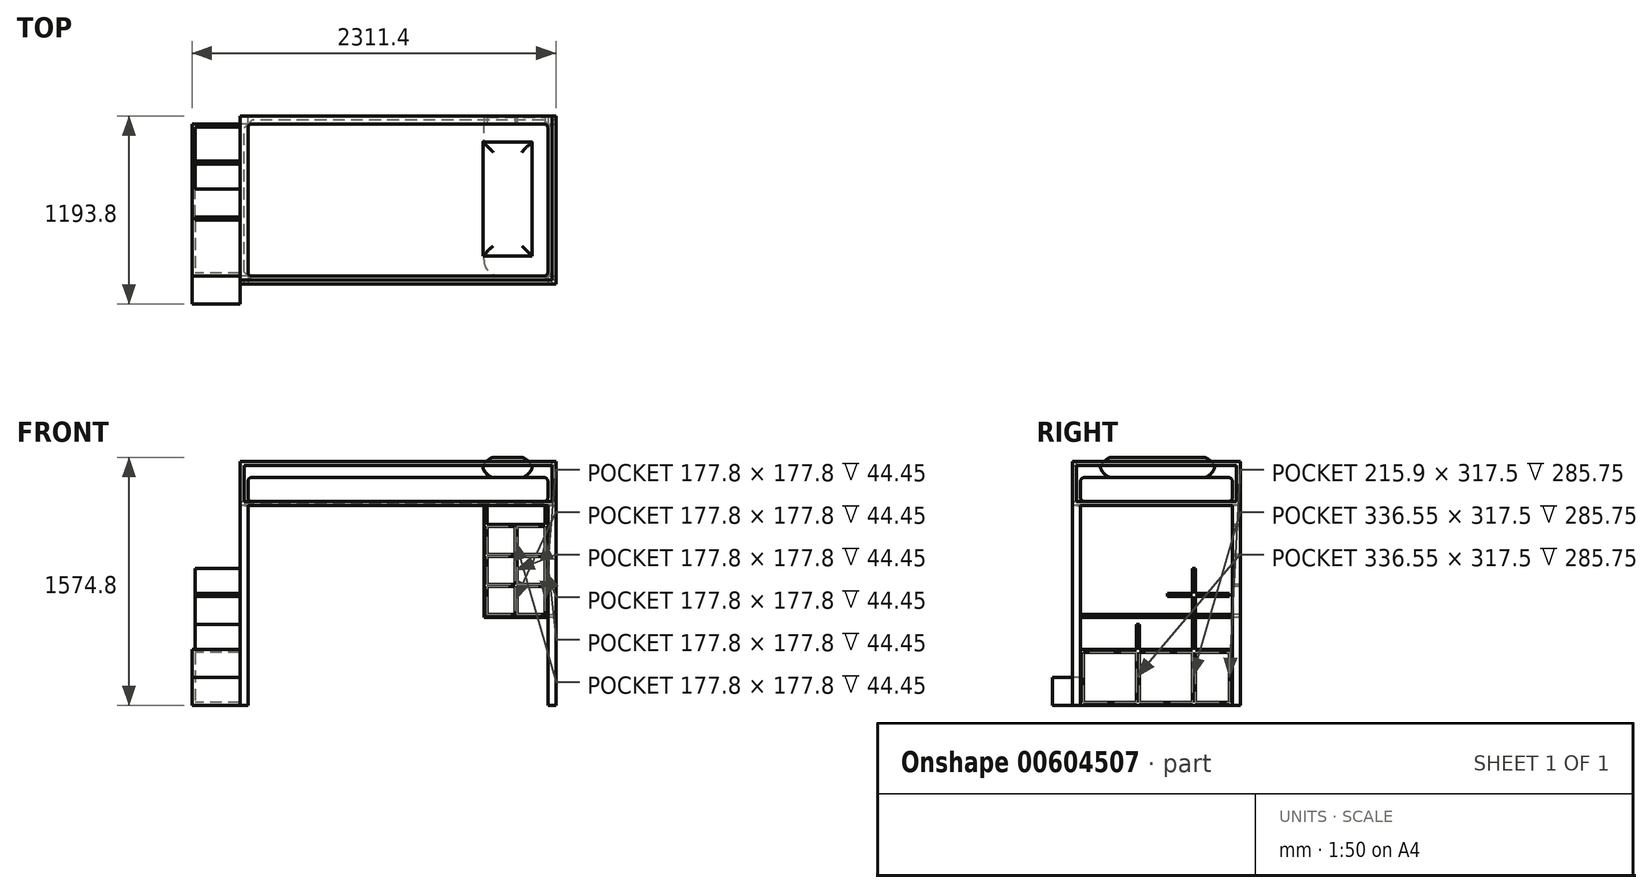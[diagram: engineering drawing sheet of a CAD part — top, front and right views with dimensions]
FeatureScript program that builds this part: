
annotation { "Feature Type Name" : "Feature", "Feature Type Description" : "" }
export const myFeature = defineFeature(function(context is Context, id is Id, definition is map)
    precondition{}
    {
        {
            var Q0;
            Q0=qCreatedBy(makeId("Top.planeOp"),FACE);
            var sketch = newSketch(context, id + "F0", { "sketchPlane" : qUnion([Q0])});
            skLineSegment(sketch, "E0.bottom", {"start": v(-952.5, 482.6) * mm, "end": v(952.5, 482.6) * mm});
            skLineSegment(sketch, "E0.top", {"start": v(-952.5, -482.6) * mm, "end": v(952.5, -482.6) * mm});
            skLineSegment(sketch, "E0.left", {"start": v(-952.5, 482.6) * mm, "end": v(-952.5, -482.6) * mm});
            skLineSegment(sketch, "E0.right", {"start": v(952.5, 482.6) * mm, "end": v(952.5, -482.6) * mm});
            skPoint(sketch, "E0.middle", {"position": v(0, 0) * mm});
            skLineSegment(sketch, "E1.bottom", {"start": v(-952.5, 482.6) * mm, "end": v(-1003.3, 482.6) * mm});
            skLineSegment(sketch, "E1.top", {"start": v(-952.5, 533.4) * mm, "end": v(-1003.3, 533.4) * mm});
            skLineSegment(sketch, "E1.left", {"start": v(-952.5, 482.6) * mm, "end": v(-952.5, 533.4) * mm});
            skLineSegment(sketch, "E1.right", {"start": v(-1003.3, 482.6) * mm, "end": v(-1003.3, 533.4) * mm});
            skLineSegment(sketch, "E2.bottom", {"start": v(-952.5, -482.6) * mm, "end": v(-1003.3, -482.6) * mm});
            skLineSegment(sketch, "E2.top", {"start": v(-952.5, -533.4) * mm, "end": v(-1003.3, -533.4) * mm});
            skLineSegment(sketch, "E2.left", {"start": v(-952.5, -482.6) * mm, "end": v(-952.5, -533.4) * mm});
            skLineSegment(sketch, "E2.right", {"start": v(-1003.3, -482.6) * mm, "end": v(-1003.3, -533.4) * mm});
            skLineSegment(sketch, "E3.bottom", {"start": v(952.5, 482.6) * mm, "end": v(1003.3, 482.6) * mm});
            skLineSegment(sketch, "E3.top", {"start": v(952.5, 533.4) * mm, "end": v(1003.3, 533.4) * mm});
            skLineSegment(sketch, "E3.left", {"start": v(952.5, 482.6) * mm, "end": v(952.5, 533.4) * mm});
            skLineSegment(sketch, "E3.right", {"start": v(1003.3, 482.6) * mm, "end": v(1003.3, 533.4) * mm});
            skLineSegment(sketch, "E4.bottom", {"start": v(952.5, -482.6) * mm, "end": v(1003.3, -482.6) * mm});
            skLineSegment(sketch, "E4.top", {"start": v(952.5, -533.4) * mm, "end": v(1003.3, -533.4) * mm});
            skLineSegment(sketch, "E4.left", {"start": v(952.5, -482.6) * mm, "end": v(952.5, -533.4) * mm});
            skLineSegment(sketch, "E4.right", {"start": v(1003.3, -482.6) * mm, "end": v(1003.3, -533.4) * mm});
            skSolve(sketch);
        }
        {
            var Q0;
            Q0=makeQuery(id+"F0.imprint","IMPRINT",FACE,{"disambiguationData":[TD([[makeQuery(id+"F0.imprint","IMPRINT",EDGE,{"derivedFrom":sQuery(id+"F0.wireOp",EDGE,"E1.bottom")}),-1.0]])]});
            var Q1;
            Q1=makeQuery(id+"F0.imprint","IMPRINT",FACE,{"disambiguationData":[TD([[makeQuery(id+"F0.imprint","IMPRINT",EDGE,{"derivedFrom":sQuery(id+"F0.wireOp",EDGE,"E2.bottom")}),1.0]])]});
            var Q2;
            Q2=makeQuery(id+"F0.imprint","IMPRINT",FACE,{"disambiguationData":[TD([[makeQuery(id+"F0.imprint","IMPRINT",EDGE,{"derivedFrom":sQuery(id+"F0.wireOp",EDGE,"E3.bottom")}),1.0]])]});
            var Q3;
            Q3=makeQuery(id+"F0.imprint","IMPRINT",FACE,{"disambiguationData":[TD([[makeQuery(id+"F0.imprint","IMPRINT",EDGE,{"derivedFrom":sQuery(id+"F0.wireOp",EDGE,"E4.bottom")}),-1.0]])]});
            extrude(context, id + "F1", {"entities" : qUnion([Q0, Q1, Q2, Q3]), "depth" : 1270 * mm});
        }
        {
            var Q0;
            Q0=makeQuery(id+"F1.opExtrude","SWEPT_FACE",FACE,{"disambiguationData":[OSD([sQuery(id+"F0.wireOp",EDGE,"E1.right")])]});
            cPlane(context, id + "F2", {"entities" : qUnion([Q0]), "cplaneType" : CPlaneType.OFFSET, "offset" : 304.8 * mm, "width" : 152.4 * mm, "height" : 152.4 * mm});
        }
        {
            var Q0;
            Q0=qCreatedBy(id+"F2.planeOp",FACE);
            var sketch = newSketch(context, id + "F3", { "sketchPlane" : qUnion([Q0])});
            skPoint(sketch, "E5.0", {"position": v(-482.6, 0) * mm});
            skPoint(sketch, "E6.0", {"position": v(482.6, 0) * mm});
            skLineSegment(sketch, "E7.bottom", {"start": v(-482.6, 0) * mm, "end": v(482.6, 0) * mm});
            skLineSegment(sketch, "E7.top", {"start": v(-482.6, 355.6) * mm, "end": v(482.6, 355.6) * mm});
            skLineSegment(sketch, "E7.left", {"start": v(-482.6, 0) * mm, "end": v(-482.6, 355.6) * mm});
            skLineSegment(sketch, "E7.right", {"start": v(482.6, 0) * mm, "end": v(482.6, 147.48) * mm});
            skLineSegment(sketch, "E8.bottom", {"start": v(-482.6, 355.6) * mm, "end": v(127, 355.6) * mm});
            skLineSegment(sketch, "E8.top", {"start": v(-482.6, 711.2) * mm, "end": v(127, 711.2) * mm});
            skLineSegment(sketch, "E8.left", {"start": v(-482.6, 355.6) * mm, "end": v(-482.6, 711.2) * mm});
            skLineSegment(sketch, "E8.right", {"start": v(127, 355.6) * mm, "end": v(127, 711.2) * mm});
            skLineSegment(sketch, "E9.bottom", {"start": v(-482.6, 711.2) * mm, "end": v(-228.6, 711.2) * mm});
            skLineSegment(sketch, "E9.top", {"start": v(-482.6, 1066.8) * mm, "end": v(-228.6, 1066.8) * mm});
            skLineSegment(sketch, "E9.left", {"start": v(-482.6, 711.2) * mm, "end": v(-482.6, 1066.8) * mm});
            skLineSegment(sketch, "E9.right", {"start": v(-228.6, 711.2) * mm, "end": v(-228.6, 1066.8) * mm});
            skLineSegment(sketch, "E10.bottom", {"start": v(127, 355.6) * mm, "end": v(304.8, 355.6) * mm});
            skLineSegment(sketch, "E10.top", {"start": v(127, 533.4) * mm, "end": v(304.8, 533.4) * mm});
            skLineSegment(sketch, "E10.left", {"start": v(127, 355.6) * mm, "end": v(127, 533.4) * mm});
            skLineSegment(sketch, "E10.right", {"start": v(304.8, 355.6) * mm, "end": v(304.8, 533.4) * mm});
            skLineSegment(sketch, "E11.bottom", {"start": v(482.6, 0) * mm, "end": v(660.4, 0) * mm});
            skLineSegment(sketch, "E11.top", {"start": v(482.6, 177.8) * mm, "end": v(660.4, 177.8) * mm});
            skLineSegment(sketch, "E11.left", {"start": v(482.6, 0) * mm, "end": v(482.6, 177.8) * mm});
            skLineSegment(sketch, "E11.right", {"start": v(660.4, 0) * mm, "end": v(660.4, 177.8) * mm});
            skLineSegment(sketch, "E12.bottom", {"start": v(-228.6, 711.2) * mm, "end": v(-50.8, 711.2) * mm});
            skLineSegment(sketch, "E12.top", {"start": v(-228.6, 889) * mm, "end": v(-50.8, 889) * mm});
            skLineSegment(sketch, "E12.left", {"start": v(-228.6, 711.2) * mm, "end": v(-228.6, 889) * mm});
            skLineSegment(sketch, "E12.right", {"start": v(-50.8, 711.2) * mm, "end": v(-50.8, 889) * mm});
            skLineSegment(sketch, "E13", {"start": v(482.6, 355.6) * mm, "end": v(482.6, 177.8) * mm});
            skSolve(sketch);
        }
        {
            var Q0;
            Q0=makeQuery(id+"F3.imprint","IMPRINT",FACE,{"disambiguationData":[TD([[makeQuery(id+"F3.imprint","IMPRINT",EDGE,{"derivedFrom":sQuery(id+"F3.wireOp",EDGE,"E9.bottom")}),1.0]])]});
            var Q1;
            Q1=makeQuery(id+"F3.imprint","IMPRINT",FACE,{"disambiguationData":[TD([[makeQuery(id+"F3.imprint","IMPRINT",EDGE,{"derivedFrom":sQuery(id+"F3.wireOp",EDGE,"E12.bottom")}),1.0]])]});
            var Q2;
            Q2=makeQuery(id+"F3.imprint","IMPRINT",FACE,{"disambiguationData":[TD([[makeQuery(id+"F3.imprint","IMPRINT",EDGE,{"derivedFrom":sQuery(id+"F3.wireOp",EDGE,"E8.bottom")}),1.0]])]});
            var Q3;
            Q3=makeQuery(id+"F3.imprint","IMPRINT",FACE,{"disambiguationData":[TD([[makeQuery(id+"F3.imprint","IMPRINT",EDGE,{"derivedFrom":sQuery(id+"F3.wireOp",EDGE,"E10.bottom")}),1.0]])]});
            var Q4;
            {var subQ1=sQuery(id+"F3.wireOp",EDGE,"E7.bottom");Q4=makeQuery(id+"F3.imprint","IMPRINT",FACE,{"disambiguationData":[TD([[makeQuery(id+"F3.imprint","IMPRINT",EDGE,{"derivedFrom":subQ1}),1.0]])]});}
            var Q5;
            {var subQ3=sQuery(id+"F3.wireOp",EDGE,"E11.bottom");Q5=makeQuery(id+"F3.imprint","IMPRINT",FACE,{"disambiguationData":[TD([[makeQuery(id+"F3.imprint","IMPRINT",EDGE,{"derivedFrom":subQ3}),1.0]])]});}
            extrude(context, id + "F4", {"entities" : qUnion([Q0, Q1, Q2, Q3, Q4, Q5]), "oppositeDirection" : true, "depth" : 19.05 * mm});
        }
        {
            var Q0;
            Q0=makeQuery(id+"F4.opExtrude","CAP_FACE",FACE,{"disambiguationData":[OSD([sQuery(id+"F3.wireOp",EDGE,"E7.bottom"),sQuery(id+"F3.wireOp",EDGE,"E7.top"),sQuery(id+"F3.wireOp",EDGE,"E7.left"),sQuery(id+"F3.wireOp",EDGE,"E8.top"),sQuery(id+"F3.wireOp",EDGE,"E8.left"),sQuery(id+"F3.wireOp",EDGE,"E8.right"),sQuery(id+"F3.wireOp",EDGE,"E9.top"),sQuery(id+"F3.wireOp",EDGE,"E9.left"),sQuery(id+"F3.wireOp",EDGE,"E9.right"),sQuery(id+"F3.wireOp",EDGE,"E10.top"),sQuery(id+"F3.wireOp",EDGE,"E10.right"),sQuery(id+"F3.wireOp",EDGE,"E11.bottom"),sQuery(id+"F3.wireOp",EDGE,"E11.top"),sQuery(id+"F3.wireOp",EDGE,"E11.right"),sQuery(id+"F3.wireOp",EDGE,"E12.top"),sQuery(id+"F3.wireOp",EDGE,"E12.right"),sQuery(id+"F3.wireOp",EDGE,"E13")])],"isStart":false});
            var sketch = newSketch(context, id + "F5", { "sketchPlane" : qUnion([Q0])});
            skLineSegment(sketch, "E14.0", {"start": v(-463.55, 19.05) * mm, "end": v(463.55, 19.05) * mm});
            skLineSegment(sketch, "E14.1", {"start": v(69.85, 869.95) * mm, "end": v(69.85, 692.15) * mm});
            skLineSegment(sketch, "E14.2", {"start": v(247.65, 869.95) * mm, "end": v(69.85, 869.95) * mm});
            skLineSegment(sketch, "E14.3", {"start": v(247.65, 1047.75) * mm, "end": v(247.65, 869.95) * mm});
            skLineSegment(sketch, "E14.4", {"start": v(463.55, 1047.75) * mm, "end": v(247.65, 1047.75) * mm});
            skLineSegment(sketch, "E14.5", {"start": v(69.85, 692.15) * mm, "end": v(-107.95, 692.15) * mm});
            skLineSegment(sketch, "E14.6", {"start": v(463.55, 19.05) * mm, "end": v(463.55, 1047.75) * mm});
            skLineSegment(sketch, "E14.7", {"start": v(-107.95, 692.15) * mm, "end": v(-107.95, 514.35) * mm});
            skLineSegment(sketch, "E14.8", {"start": v(-107.95, 514.35) * mm, "end": v(-285.75, 514.35) * mm});
            skLineSegment(sketch, "E14.9", {"start": v(-285.75, 514.35) * mm, "end": v(-285.75, 336.55) * mm});
            skLineSegment(sketch, "E14.10", {"start": v(-285.75, 336.55) * mm, "end": v(-463.55, 336.55) * mm});
            skLineSegment(sketch, "E14.11", {"start": v(-463.55, 336.55) * mm, "end": v(-463.55, 19.05) * mm});
            skLineSegment(sketch, "E15.0.0", {"start": v(482.6, 0) * mm, "end": v(482.6, 1066.8) * mm});
            skLineSegment(sketch, "E15.0.1", {"start": v(482.6, 1066.8) * mm, "end": v(228.6, 1066.8) * mm});
            skLineSegment(sketch, "E15.0.2", {"start": v(228.6, 1066.8) * mm, "end": v(228.6, 889) * mm});
            skLineSegment(sketch, "E15.0.3", {"start": v(228.6, 889) * mm, "end": v(50.8, 889) * mm});
            skLineSegment(sketch, "E15.0.4", {"start": v(50.8, 889) * mm, "end": v(50.8, 711.2) * mm});
            skLineSegment(sketch, "E15.0.5", {"start": v(50.8, 711.2) * mm, "end": v(-127, 711.2) * mm});
            skLineSegment(sketch, "E15.0.6", {"start": v(-127, 711.2) * mm, "end": v(-127, 533.4) * mm});
            skLineSegment(sketch, "E15.0.7", {"start": v(-127, 533.4) * mm, "end": v(-304.8, 533.4) * mm});
            skLineSegment(sketch, "E15.0.8", {"start": v(-304.8, 533.4) * mm, "end": v(-304.8, 355.6) * mm});
            skLineSegment(sketch, "E15.0.9", {"start": v(-304.8, 355.6) * mm, "end": v(-482.6, 355.6) * mm});
            skLineSegment(sketch, "E15.0.10", {"start": v(-482.6, 355.6) * mm, "end": v(-482.6, 177.8) * mm});
            skLineSegment(sketch, "E15.0.11", {"start": v(-482.6, 177.8) * mm, "end": v(-660.4, 177.8) * mm});
            skLineSegment(sketch, "E15.0.12", {"start": v(-660.4, 177.8) * mm, "end": v(-660.4, 0) * mm});
            skLineSegment(sketch, "E15.0.13", {"start": v(-660.4, 0) * mm, "end": v(482.6, 0) * mm});
            skSolve(sketch);
        }
        {
            var Q0;
            Q0=makeQuery(id+"F5.imprint","IMPRINT",FACE,{"disambiguationData":[TD([[makeQuery(id+"F5.imprint","IMPRINT",EDGE,{"derivedFrom":sQuery(id+"F5.wireOp",EDGE,"E14.0")}),-1.0]])]});
            extrude(context, id + "F6", {"entities" : qUnion([Q0]), "operationType" : NewBodyOperationType.ADD, "depth" : 285.75 * mm});
        }
        {
            var Q0;
            Q0=makeQuery(id+"F4.opExtrude","CAP_FACE",FACE,{"disambiguationData":[OSD([sQuery(id+"F3.wireOp",EDGE,"E7.bottom"),sQuery(id+"F3.wireOp",EDGE,"E7.top"),sQuery(id+"F3.wireOp",EDGE,"E7.left"),sQuery(id+"F3.wireOp",EDGE,"E8.top"),sQuery(id+"F3.wireOp",EDGE,"E8.left"),sQuery(id+"F3.wireOp",EDGE,"E8.right"),sQuery(id+"F3.wireOp",EDGE,"E9.top"),sQuery(id+"F3.wireOp",EDGE,"E9.left"),sQuery(id+"F3.wireOp",EDGE,"E9.right"),sQuery(id+"F3.wireOp",EDGE,"E10.top"),sQuery(id+"F3.wireOp",EDGE,"E10.right"),sQuery(id+"F3.wireOp",EDGE,"E11.bottom"),sQuery(id+"F3.wireOp",EDGE,"E11.top"),sQuery(id+"F3.wireOp",EDGE,"E11.right"),sQuery(id+"F3.wireOp",EDGE,"E12.top"),sQuery(id+"F3.wireOp",EDGE,"E12.right"),sQuery(id+"F3.wireOp",EDGE,"E13")])],"isStart":false});
            var sketch = newSketch(context, id + "F7", { "sketchPlane" : qUnion([Q0])});
            skLineSegment(sketch, "E16.bottom", {"start": v(-285.75, 336.55) * mm, "end": v(463.55, 336.55) * mm});
            skLineSegment(sketch, "E16.top", {"start": v(-285.75, 355.6) * mm, "end": v(463.55, 355.6) * mm});
            skLineSegment(sketch, "E16.left", {"start": v(-285.75, 336.55) * mm, "end": v(-285.75, 355.6) * mm});
            skLineSegment(sketch, "E16.right", {"start": v(463.55, 336.55) * mm, "end": v(463.55, 355.6) * mm});
            skLineSegment(sketch, "E17.bottom", {"start": v(-107.95, 514.35) * mm, "end": v(-127, 514.35) * mm});
            skLineSegment(sketch, "E17.top", {"start": v(-107.95, 19.05) * mm, "end": v(-127, 19.05) * mm});
            skLineSegment(sketch, "E17.left", {"start": v(-107.95, 514.35) * mm, "end": v(-107.95, 19.05) * mm});
            skLineSegment(sketch, "E17.right", {"start": v(-127, 514.35) * mm, "end": v(-127, 19.05) * mm});
            skLineSegment(sketch, "E18.bottom", {"start": v(247.65, 869.95) * mm, "end": v(228.6, 869.95) * mm});
            skLineSegment(sketch, "E18.top", {"start": v(247.65, 19.05) * mm, "end": v(228.6, 19.05) * mm});
            skLineSegment(sketch, "E18.left", {"start": v(247.65, 869.95) * mm, "end": v(247.65, 19.05) * mm});
            skLineSegment(sketch, "E18.right", {"start": v(228.6, 869.95) * mm, "end": v(228.6, 19.05) * mm});
            skLineSegment(sketch, "E19.bottom", {"start": v(69.85, 692.15) * mm, "end": v(463.55, 692.15) * mm});
            skLineSegment(sketch, "E19.top", {"start": v(69.85, 711.2) * mm, "end": v(463.55, 711.2) * mm});
            skLineSegment(sketch, "E19.left", {"start": v(69.85, 692.15) * mm, "end": v(69.85, 711.2) * mm});
            skLineSegment(sketch, "E19.right", {"start": v(463.55, 692.15) * mm, "end": v(463.55, 711.2) * mm});
            skSolve(sketch);
        }
        {
            var Q0;
            Q0=qSketchRegion(id+"F7",true);
            extrude(context, id + "F8", {"entities" : qUnion([Q0]), "operationType" : NewBodyOperationType.ADD, "depth" : 285.75 * mm});
        }
        {
            var Q0;
            Q0=makeQuery(id+"F1.opExtrude","CAP_FACE",FACE,{"disambiguationData":[OSD([sQuery(id+"F0.wireOp",EDGE,"E1.bottom"),sQuery(id+"F0.wireOp",EDGE,"E1.top"),sQuery(id+"F0.wireOp",EDGE,"E1.left"),sQuery(id+"F0.wireOp",EDGE,"E1.right")])],"isStart":false});
            var sketch = newSketch(context, id + "F9", { "sketchPlane" : qUnion([Q0])});
            skPoint(sketch, "E20.0", {"position": v(1003.3, -533.4) * mm});
            skPoint(sketch, "E21.0", {"position": v(-1003.3, 533.4) * mm});
            skLineSegment(sketch, "E22.bottom", {"start": v(-1003.3, 533.4) * mm, "end": v(1003.3, 533.4) * mm});
            skLineSegment(sketch, "E22.top", {"start": v(-1003.3, -533.4) * mm, "end": v(1003.3, -533.4) * mm});
            skLineSegment(sketch, "E22.left", {"start": v(-1003.3, 533.4) * mm, "end": v(-1003.3, -533.4) * mm});
            skLineSegment(sketch, "E22.right", {"start": v(1003.3, 533.4) * mm, "end": v(1003.3, -533.4) * mm});
            skLineSegment(sketch, "E23.0.0", {"start": v(1003.3, -482.6) * mm, "end": v(952.5, -482.6) * mm});
            skLineSegment(sketch, "E23.0.1", {"start": v(952.5, -482.6) * mm, "end": v(952.5, -533.4) * mm});
            skLineSegment(sketch, "E23.0.2", {"start": v(952.5, -533.4) * mm, "end": v(1003.3, -533.4) * mm});
            skLineSegment(sketch, "E23.0.3", {"start": v(1003.3, -533.4) * mm, "end": v(1003.3, -482.6) * mm});
            skLineSegment(sketch, "E24.0.0", {"start": v(1003.3, 533.4) * mm, "end": v(952.5, 533.4) * mm});
            skLineSegment(sketch, "E24.0.1", {"start": v(952.5, 533.4) * mm, "end": v(952.5, 482.6) * mm});
            skLineSegment(sketch, "E24.0.2", {"start": v(952.5, 482.6) * mm, "end": v(1003.3, 482.6) * mm});
            skLineSegment(sketch, "E24.0.3", {"start": v(1003.3, 482.6) * mm, "end": v(1003.3, 533.4) * mm});
            skLineSegment(sketch, "E25.0.0", {"start": v(-952.5, -533.4) * mm, "end": v(-952.5, -482.6) * mm});
            skLineSegment(sketch, "E25.0.1", {"start": v(-952.5, -482.6) * mm, "end": v(-1003.3, -482.6) * mm});
            skLineSegment(sketch, "E25.0.2", {"start": v(-1003.3, -482.6) * mm, "end": v(-1003.3, -533.4) * mm});
            skLineSegment(sketch, "E25.0.3", {"start": v(-1003.3, -533.4) * mm, "end": v(-952.5, -533.4) * mm});
            skLineSegment(sketch, "E26.0.0", {"start": v(-952.5, 482.6) * mm, "end": v(-952.5, 533.4) * mm});
            skLineSegment(sketch, "E26.0.1", {"start": v(-952.5, 533.4) * mm, "end": v(-1003.3, 533.4) * mm});
            skLineSegment(sketch, "E26.0.2", {"start": v(-1003.3, 533.4) * mm, "end": v(-1003.3, 482.6) * mm});
            skLineSegment(sketch, "E26.0.3", {"start": v(-1003.3, 482.6) * mm, "end": v(-952.5, 482.6) * mm});
            skPoint(sketch, "E27.firstSnap0", {"position": v(952.5, -508) * mm});
            skPoint(sketch, "E27.firstSnap1", {"position": v(977.9, -482.6) * mm});
            skPoint(sketch, "E27.oppositeSnap0", {"position": v(-1003.3, 508) * mm});
            skPoint(sketch, "E27.oppositeSnap1", {"position": v(-977.9, 533.4) * mm});
            skLineSegment(sketch, "E27.bottom", {"start": v(977.9, -508) * mm, "end": v(-977.9, -508) * mm});
            skLineSegment(sketch, "E27.top", {"start": v(977.9, 508) * mm, "end": v(-977.9, 508) * mm});
            skLineSegment(sketch, "E27.left", {"start": v(977.9, -508) * mm, "end": v(977.9, 508) * mm});
            skLineSegment(sketch, "E27.right", {"start": v(-977.9, -508) * mm, "end": v(-977.9, 508) * mm});
            skSolve(sketch);
        }
        {
            var Q0;
            Q0=qSketchRegion(id+"F9",true);
            extrude(context, id + "F10", {"entities" : qUnion([Q0]), "depth" : 25.4 * mm});
        }
        {
            var Q0;
            Q0=makeQuery(id+"F10.opExtrude","CAP_FACE",FACE,{"disambiguationData":[OSD([sQuery(id+"F9.wireOp",EDGE,"E22.bottom"),sQuery(id+"F9.wireOp",EDGE,"E22.top"),sQuery(id+"F9.wireOp",EDGE,"E22.left"),sQuery(id+"F9.wireOp",EDGE,"E22.right")])],"isStart":false});
            var sketch = newSketch(context, id + "F11", { "sketchPlane" : qUnion([Q0])});
            skPoint(sketch, "E28.0", {"position": v(-952.5, 482.6) * mm});
            skPoint(sketch, "E29.0", {"position": v(952.5, -482.6) * mm});
            skLineSegment(sketch, "E30.bottom", {"start": v(-952.5, 482.6) * mm, "end": v(952.5, 482.6) * mm});
            skLineSegment(sketch, "E30.top", {"start": v(-952.5, -482.6) * mm, "end": v(952.5, -482.6) * mm});
            skLineSegment(sketch, "E30.left", {"start": v(-952.5, 482.6) * mm, "end": v(-952.5, -482.6) * mm});
            skLineSegment(sketch, "E30.right", {"start": v(952.5, 482.6) * mm, "end": v(952.5, -482.6) * mm});
            skSolve(sketch);
        }
        {
            var Q0;
            Q0=makeQuery(id+"F11.imprint","IMPRINT",FACE,{"disambiguationData":[TD([[makeQuery(id+"F11.imprint","IMPRINT",EDGE,{"derivedFrom":sQuery(id+"F11.wireOp",EDGE,"E30.bottom")}),-1.0]])]});
            extrude(context, id + "F12", {"entities" : qUnion([Q0]), "depth" : 152.4 * mm});
        }
        {
            var Q0;
            Q0=makeQuery(id+"F12.opExtrude","SWEPT_EDGE",EDGE,{"disambiguationData":[OSD([sQuery(id+"F11.wireOp",EDGE,"E30.top"),sQuery(id+"F11.wireOp",EDGE,"E30.left")])]});
            var Q1;
            Q1=makeQuery(id+"F12.opExtrude","SWEPT_EDGE",EDGE,{"disambiguationData":[OSD([sQuery(id+"F11.wireOp",EDGE,"E30.top"),sQuery(id+"F11.wireOp",EDGE,"E30.right")])]});
            var Q2;
            Q2=makeQuery(id+"F12.opExtrude","SWEPT_EDGE",EDGE,{"disambiguationData":[OSD([sQuery(id+"F11.wireOp",EDGE,"E30.bottom"),sQuery(id+"F11.wireOp",EDGE,"E30.right")])]});
            var Q3;
            Q3=makeQuery(id+"F12.opExtrude","SWEPT_EDGE",EDGE,{"disambiguationData":[OSD([sQuery(id+"F11.wireOp",EDGE,"E30.bottom"),sQuery(id+"F11.wireOp",EDGE,"E30.left")])]});
            var Q4;
            Q4=makeQuery(id+"F12.opExtrude","CAP_EDGE",EDGE,{"disambiguationData":[OSD([sQuery(id+"F11.wireOp",EDGE,"E30.left")])],"isStart":false});
            var Q5;
            Q5=makeQuery(id+"F12.opExtrude","CAP_EDGE",EDGE,{"disambiguationData":[OSD([sQuery(id+"F11.wireOp",EDGE,"E30.bottom")])],"isStart":false});
            var Q6;
            Q6=makeQuery(id+"F12.opExtrude","CAP_EDGE",EDGE,{"disambiguationData":[OSD([sQuery(id+"F11.wireOp",EDGE,"E30.right")])],"isStart":false});
            var Q7;
            Q7=makeQuery(id+"F12.opExtrude","CAP_EDGE",EDGE,{"disambiguationData":[OSD([sQuery(id+"F11.wireOp",EDGE,"E30.top")])],"isStart":false});
            var Q8;
            Q8=makeQuery(id+"F12.opExtrude","CAP_EDGE",EDGE,{"disambiguationData":[OSD([sQuery(id+"F11.wireOp",EDGE,"E30.top")])],"isStart":true});
            var Q9;
            Q9=makeQuery(id+"F12.opExtrude","CAP_EDGE",EDGE,{"disambiguationData":[OSD([sQuery(id+"F11.wireOp",EDGE,"E30.right")])],"isStart":true});
            var Q10;
            Q10=makeQuery(id+"F12.opExtrude","CAP_EDGE",EDGE,{"disambiguationData":[OSD([sQuery(id+"F11.wireOp",EDGE,"E30.bottom")])],"isStart":true});
            var Q11;
            Q11=makeQuery(id+"F12.opExtrude","CAP_EDGE",EDGE,{"disambiguationData":[OSD([sQuery(id+"F11.wireOp",EDGE,"E30.left")])],"isStart":true});
            fillet(context, id + "F13", {"entities" : qUnion([Q0, Q1, Q2, Q3, Q4, Q5, Q6, Q7, Q8, Q9, Q10, Q11]), "radius" : 25.4 * mm, "tangentPropagation" : true, "allowEdgeOverflow" : false});
        }
        {
            var Q0;
            Q0=makeQuery(id+"F10.opExtrude","CAP_FACE",FACE,{"disambiguationData":[OSD([sQuery(id+"F9.wireOp",EDGE,"E22.bottom"),sQuery(id+"F9.wireOp",EDGE,"E22.top"),sQuery(id+"F9.wireOp",EDGE,"E22.left"),sQuery(id+"F9.wireOp",EDGE,"E22.right"),sQuery(id+"F9.wireOp",EDGE,"E23.0.2"),sQuery(id+"F9.wireOp",EDGE,"E23.0.3"),sQuery(id+"F9.wireOp",EDGE,"E24.0.0"),sQuery(id+"F9.wireOp",EDGE,"E24.0.3"),sQuery(id+"F9.wireOp",EDGE,"E25.0.2"),sQuery(id+"F9.wireOp",EDGE,"E25.0.3"),sQuery(id+"F9.wireOp",EDGE,"E26.0.1"),sQuery(id+"F9.wireOp",EDGE,"E26.0.2"),sQuery(id+"F9.wireOp",EDGE,"E27.bottom"),sQuery(id+"F9.wireOp",EDGE,"E27.top"),sQuery(id+"F9.wireOp",EDGE,"E27.left"),sQuery(id+"F9.wireOp",EDGE,"E27.right")])],"isStart":true});
            var sketch = newSketch(context, id + "F14", { "sketchPlane" : qUnion([Q0])});
            skLineSegment(sketch, "E31.0", {"start": v(977.9, 508) * mm, "end": v(-977.9, 508) * mm});
            skLineSegment(sketch, "E32.0", {"start": v(-977.9, 508) * mm, "end": v(-977.9, -508) * mm});
            skLineSegment(sketch, "E33", {"start": v(-977.9, 508) * mm, "end": v(-927.1, 508) * mm});
            skLineSegment(sketch, "E34", {"start": v(-927.1, 508) * mm, "end": v(-977.9, 457.2) * mm});
            skLineSegment(sketch, "E35", {"start": v(-977.9, 457.2) * mm, "end": v(-977.9, 508) * mm});
            skLineSegment(sketch, "E36", {"start": v(-977.9, -508) * mm, "end": v(-977.9, -457.2) * mm});
            skLineSegment(sketch, "E37", {"start": v(-977.9, -457.2) * mm, "end": v(-927.1, -508) * mm});
            skLineSegment(sketch, "E38", {"start": v(-927.1, -508) * mm, "end": v(-977.9, -508) * mm});
            skLineSegment(sketch, "E39", {"start": v(977.9, -508) * mm, "end": v(927.1, -508) * mm});
            skLineSegment(sketch, "E40", {"start": v(927.1, -508) * mm, "end": v(977.9, -457.2) * mm});
            skLineSegment(sketch, "E41", {"start": v(977.9, -457.2) * mm, "end": v(977.9, -508) * mm});
            skLineSegment(sketch, "E42", {"start": v(977.9, 508) * mm, "end": v(927.1, 508) * mm});
            skLineSegment(sketch, "E43", {"start": v(927.1, 508) * mm, "end": v(977.9, 457.2) * mm});
            skLineSegment(sketch, "E44", {"start": v(977.9, 457.2) * mm, "end": v(977.9, 508) * mm});
            skLineSegment(sketch, "E45", {"start": v(927.1, 508) * mm, "end": v(977.9, 508) * mm});
            skLineSegment(sketch, "E46", {"start": v(977.9, 508) * mm, "end": v(977.9, 457.2) * mm});
            skSolve(sketch);
        }
        {
            var Q0;
            Q0=qSketchRegion(id+"F14",true);
            extrude(context, id + "F15", {"entities" : qUnion([Q0]), "operationType" : NewBodyOperationType.ADD, "oppositeDirection" : true, "depth" : 6.35 * mm});
        }
        {
            var Q0;
            Q0=makeQuery(id+"F15.opExtrude","CAP_FACE",FACE,{"disambiguationData":[OSD([sQuery(id+"F14.wireOp",EDGE,"E33"),sQuery(id+"F14.wireOp",EDGE,"E34"),sQuery(id+"F14.wireOp",EDGE,"E35")])],"isStart":false});
            var sketch = newSketch(context, id + "F16", { "sketchPlane" : qUnion([Q0])});
            skLineSegment(sketch, "E47.0.0", {"start": v(-977.9, 457.2) * mm, "end": v(-927.1, 508) * mm});
            skLineSegment(sketch, "E47.0.1", {"start": v(-927.1, 508) * mm, "end": v(-977.9, 508) * mm});
            skLineSegment(sketch, "E47.0.2", {"start": v(-977.9, 508) * mm, "end": v(-977.9, 457.2) * mm});
            skLineSegment(sketch, "E48.0.0", {"start": v(927.1, -508) * mm, "end": v(977.9, -508) * mm});
            skLineSegment(sketch, "E48.0.1", {"start": v(977.9, -508) * mm, "end": v(977.9, -457.2) * mm});
            skLineSegment(sketch, "E48.0.2", {"start": v(977.9, -457.2) * mm, "end": v(927.1, -508) * mm});
            skLineSegment(sketch, "E49.bottom", {"start": v(-977.9, 508) * mm, "end": v(977.9, 508) * mm});
            skLineSegment(sketch, "E49.top", {"start": v(-977.9, -508) * mm, "end": v(977.9, -508) * mm});
            skLineSegment(sketch, "E49.left", {"start": v(-977.9, 508) * mm, "end": v(-977.9, -508) * mm});
            skLineSegment(sketch, "E49.right", {"start": v(977.9, 508) * mm, "end": v(977.9, -508) * mm});
            skSolve(sketch);
        }
        {
            var Q0;
            Q0=qSketchRegion(id+"F16",true);
            extrude(context, id + "F17", {"entities" : qUnion([Q0]), "depth" : 19.05 * mm});
        }
        {
            var Q0;
            Q0=makeQuery(id+"F10.opExtrude","CAP_FACE",FACE,{"disambiguationData":[OSD([sQuery(id+"F9.wireOp",EDGE,"E22.bottom"),sQuery(id+"F9.wireOp",EDGE,"E22.top"),sQuery(id+"F9.wireOp",EDGE,"E22.left"),sQuery(id+"F9.wireOp",EDGE,"E22.right"),sQuery(id+"F9.wireOp",EDGE,"E23.0.2"),sQuery(id+"F9.wireOp",EDGE,"E23.0.3"),sQuery(id+"F9.wireOp",EDGE,"E24.0.0"),sQuery(id+"F9.wireOp",EDGE,"E24.0.3"),sQuery(id+"F9.wireOp",EDGE,"E25.0.2"),sQuery(id+"F9.wireOp",EDGE,"E25.0.3"),sQuery(id+"F9.wireOp",EDGE,"E26.0.1"),sQuery(id+"F9.wireOp",EDGE,"E26.0.2"),sQuery(id+"F9.wireOp",EDGE,"E27.bottom"),sQuery(id+"F9.wireOp",EDGE,"E27.top"),sQuery(id+"F9.wireOp",EDGE,"E27.left"),sQuery(id+"F9.wireOp",EDGE,"E27.right")])],"isStart":false});
            var sketch = newSketch(context, id + "F18", { "sketchPlane" : qUnion([Q0])});
            skLineSegment(sketch, "E50.bottom", {"start": v(1003.3, -533.4) * mm, "end": v(977.9, -533.4) * mm});
            skLineSegment(sketch, "E50.top", {"start": v(1003.3, -508) * mm, "end": v(977.9, -508) * mm});
            skLineSegment(sketch, "E50.left", {"start": v(1003.3, -533.4) * mm, "end": v(1003.3, -508) * mm});
            skLineSegment(sketch, "E50.right", {"start": v(977.9, -533.4) * mm, "end": v(977.9, -508) * mm});
            skLineSegment(sketch, "E51.bottom", {"start": v(1003.3, 533.4) * mm, "end": v(977.9, 533.4) * mm});
            skLineSegment(sketch, "E51.top", {"start": v(1003.3, 508) * mm, "end": v(977.9, 508) * mm});
            skLineSegment(sketch, "E51.left", {"start": v(1003.3, 533.4) * mm, "end": v(1003.3, 508) * mm});
            skLineSegment(sketch, "E51.right", {"start": v(977.9, 533.4) * mm, "end": v(977.9, 508) * mm});
            skLineSegment(sketch, "E52.bottom", {"start": v(-1003.3, -533.4) * mm, "end": v(-977.9, -533.4) * mm});
            skLineSegment(sketch, "E52.top", {"start": v(-1003.3, -508) * mm, "end": v(-977.9, -508) * mm});
            skLineSegment(sketch, "E52.left", {"start": v(-1003.3, -533.4) * mm, "end": v(-1003.3, -508) * mm});
            skLineSegment(sketch, "E52.right", {"start": v(-977.9, -533.4) * mm, "end": v(-977.9, -508) * mm});
            skSolve(sketch);
        }
        {
            var Q0;
            Q0=qSketchRegion(id+"F18",true);
            extrude(context, id + "F19", {"entities" : qUnion([Q0]), "operationType" : NewBodyOperationType.ADD, "depth" : 254 * mm});
        }
        {
            var Q0;
            Q0=makeQuery(id+"F19.opExtrude","CAP_FACE",FACE,{"disambiguationData":[OSD([sQuery(id+"F18.wireOp",EDGE,"E51.bottom"),sQuery(id+"F18.wireOp",EDGE,"E51.top"),sQuery(id+"F18.wireOp",EDGE,"E51.left"),sQuery(id+"F18.wireOp",EDGE,"E51.right")])],"isStart":false});
            var sketch = newSketch(context, id + "F20", { "sketchPlane" : qUnion([Q0])});
            skLineSegment(sketch, "E53.bottom", {"start": v(977.9, 508) * mm, "end": v(1003.3, 508) * mm});
            skLineSegment(sketch, "E53.top", {"start": v(977.9, -508) * mm, "end": v(1003.3, -508) * mm});
            skLineSegment(sketch, "E53.left", {"start": v(977.9, 508) * mm, "end": v(977.9, -508) * mm});
            skLineSegment(sketch, "E53.right", {"start": v(1003.3, 508) * mm, "end": v(1003.3, -508) * mm});
            skSolve(sketch);
        }
        {
            var Q0;
            Q0=qSketchRegion(id+"F20",true);
            extrude(context, id + "F21", {"entities" : qUnion([Q0]), "operationType" : NewBodyOperationType.ADD, "oppositeDirection" : true, "depth" : 25.4 * mm});
        }
        {
            var Q0;
            Q0=makeQuery(id+"F21.boolean.opBoolean","MERGE",FACE,{"derivedFrom":[makeQuery(id+"F19.opExtrude","CAP_FACE",FACE,{"disambiguationData":[OSD([sQuery(id+"F18.wireOp",EDGE,"E50.bottom"),sQuery(id+"F18.wireOp",EDGE,"E50.top"),sQuery(id+"F18.wireOp",EDGE,"E50.left"),sQuery(id+"F18.wireOp",EDGE,"E50.right")])],"isStart":false}),makeQuery(id+"F19.opExtrude","CAP_FACE",FACE,{"disambiguationData":[OSD([sQuery(id+"F18.wireOp",EDGE,"E51.bottom"),sQuery(id+"F18.wireOp",EDGE,"E51.top"),sQuery(id+"F18.wireOp",EDGE,"E51.left"),sQuery(id+"F18.wireOp",EDGE,"E51.right")])],"isStart":false}),makeQuery(id+"F21.opExtrude","CAP_FACE",FACE,{"disambiguationData":[OSD([sQuery(id+"F20.wireOp",EDGE,"E53.bottom"),sQuery(id+"F20.wireOp",EDGE,"E53.top"),sQuery(id+"F20.wireOp",EDGE,"E53.left"),sQuery(id+"F20.wireOp",EDGE,"E53.right")])],"isStart":true})]});
            var sketch = newSketch(context, id + "F22", { "sketchPlane" : qUnion([Q0])});
            skPoint(sketch, "E54.0", {"position": v(-977.9, -508) * mm});
            skPoint(sketch, "E55.0", {"position": v(977.9, -533.4) * mm});
            skLineSegment(sketch, "E56.bottom", {"start": v(977.9, -533.4) * mm, "end": v(-977.9, -533.4) * mm});
            skLineSegment(sketch, "E56.top", {"start": v(977.9, -508) * mm, "end": v(-977.9, -508) * mm});
            skLineSegment(sketch, "E56.left", {"start": v(977.9, -533.4) * mm, "end": v(977.9, -508) * mm});
            skLineSegment(sketch, "E56.right", {"start": v(-977.9, -533.4) * mm, "end": v(-977.9, -508) * mm});
            skSolve(sketch);
        }
        {
            var Q0;
            Q0=makeQuery(id+"F22.imprint","IMPRINT",FACE,{"disambiguationData":[TD([[makeQuery(id+"F22.imprint","IMPRINT",EDGE,{"derivedFrom":sQuery(id+"F22.wireOp",EDGE,"E56.bottom")}),-1.0]])]});
            extrude(context, id + "F23", {"entities" : qUnion([Q0]), "operationType" : NewBodyOperationType.ADD, "oppositeDirection" : true, "depth" : 25.4 * mm});
        }
        {
            var Q0;
            Q0=makeQuery(id+"F12.opExtrude","CAP_FACE",FACE,{"disambiguationData":[OSD([sQuery(id+"F11.wireOp",EDGE,"E30.bottom"),sQuery(id+"F11.wireOp",EDGE,"E30.top"),sQuery(id+"F11.wireOp",EDGE,"E30.left"),sQuery(id+"F11.wireOp",EDGE,"E30.right")])],"isStart":false});
            var sketch = newSketch(context, id + "F24", { "sketchPlane" : qUnion([Q0])});
            skLineSegment(sketch, "E57.bottom", {"start": v(540.1, -354.77) * mm, "end": v(852, -354.77) * mm});
            skLineSegment(sketch, "E57.top", {"start": v(540.1, 369.22) * mm, "end": v(852, 369.22) * mm});
            skLineSegment(sketch, "E57.left", {"start": v(540.1, -354.77) * mm, "end": v(540.1, 369.22) * mm});
            skLineSegment(sketch, "E57.right", {"start": v(852, -354.77) * mm, "end": v(852, 369.22) * mm});
            skSolve(sketch);
        }
        {
            var Q0;
            Q0=makeQuery(id+"F24.imprint","IMPRINT",FACE,{"disambiguationData":[TD([[makeQuery(id+"F24.imprint","IMPRINT",EDGE,{"derivedFrom":sQuery(id+"F24.wireOp",EDGE,"E57.bottom")}),1.0]])]});
            extrude(context, id + "F25", {"entities" : qUnion([Q0]), "depth" : 127 * mm});
        }
        {
            var Q0;
            Q0=makeQuery(id+"F25.opExtrude","CAP_EDGE",EDGE,{"disambiguationData":[OSD([sQuery(id+"F24.wireOp",EDGE,"E57.top")])],"isStart":false});
            var Q1;
            Q1=makeQuery(id+"F25.opExtrude","CAP_EDGE",EDGE,{"disambiguationData":[OSD([sQuery(id+"F24.wireOp",EDGE,"E57.bottom")])],"isStart":false});
            var Q2;
            Q2=makeQuery(id+"F25.opExtrude","CAP_EDGE",EDGE,{"disambiguationData":[OSD([sQuery(id+"F24.wireOp",EDGE,"E57.top")])],"isStart":true});
            var Q3;
            Q3=makeQuery(id+"F25.opExtrude","CAP_EDGE",EDGE,{"disambiguationData":[OSD([sQuery(id+"F24.wireOp",EDGE,"E57.bottom")])],"isStart":true});
            var Q4;
            Q4=makeQuery(id+"F25.opExtrude","CAP_EDGE",EDGE,{"disambiguationData":[OSD([sQuery(id+"F24.wireOp",EDGE,"E57.right")])],"isStart":false});
            var Q5;
            Q5=makeQuery(id+"F25.opExtrude","CAP_EDGE",EDGE,{"disambiguationData":[OSD([sQuery(id+"F24.wireOp",EDGE,"E57.right")])],"isStart":true});
            var Q6;
            Q6=makeQuery(id+"F25.opExtrude","CAP_EDGE",EDGE,{"disambiguationData":[OSD([sQuery(id+"F24.wireOp",EDGE,"E57.left")])],"isStart":true});
            var Q7;
            Q7=makeQuery(id+"F25.opExtrude","CAP_EDGE",EDGE,{"disambiguationData":[OSD([sQuery(id+"F24.wireOp",EDGE,"E57.left")])],"isStart":false});
            fillet(context, id + "F26", {"entities" : qUnion([Q0, Q1, Q2, Q3, Q4, Q5, Q6, Q7]), "radius" : 63.5 * mm, "tangentPropagation" : true, "rho" : .25, "crossSection" : FilletCrossSection.CONIC, "allowEdgeOverflow" : false});
        }
        {
            var Q0;
            Q0=makeQuery(id+"F1.opExtrude","SWEPT_FACE",FACE,{"disambiguationData":[OSD([sQuery(id+"F0.wireOp",EDGE,"E3.bottom")])]});
            var sketch = newSketch(context, id + "F27", { "sketchPlane" : qUnion([Q0])});
            skLineSegment(sketch, "E58", {"start": v(1003.3, 0) * mm, "end": v(1003.3, 558.8) * mm});
            skLineSegment(sketch, "E59", {"start": v(1003.3, 558.8) * mm, "end": v(546.1, 558.8) * mm});
            skLineSegment(sketch, "E60", {"start": v(546.1, 558.8) * mm, "end": v(546.1, 577.85) * mm});
            skLineSegment(sketch, "E61", {"start": v(546.1, 577.85) * mm, "end": v(1003.3, 577.85) * mm});
            skLineSegment(sketch, "E62", {"start": v(1003.3, 577.85) * mm, "end": v(1003.3, 558.8) * mm});
            skSolve(sketch);
        }
        {
            var Q0;
            {var subQ0=sQuery(id+"F27.wireOp",EDGE,"E60");Q0=makeQuery(id+"F27.imprint","IMPRINT",FACE,{"disambiguationData":[TD([[makeQuery(id+"F27.imprint","IMPRINT",EDGE,{"derivedFrom":subQ0}),-1.0]])]});}
            var Q1;
            {var subQ0=sQuery(id+"F27.wireOp",EDGE,"E62");Q1=makeQuery(id+"F27.imprint","IMPRINT",FACE,{"disambiguationData":[TD([[makeQuery(id+"F27.imprint","IMPRINT",EDGE,{"derivedFrom":subQ0}),-1.0]])]});}
            extrude(context, id + "F28", {"entities" : qUnion([Q0, Q1]), "depth" : 965.2 * mm});
        }
        {
            var Q0;
            Q0=makeQuery(id+"F28.opExtrude","CAP_EDGE",EDGE,{"disambiguationData":[OSD([sQuery(id+"F27.wireOp",EDGE,"E60")])],"isStart":false});
            fillet(context, id + "F29", {"entities" : qUnion([Q0]), "radius" : 101.6 * mm, "tangentPropagation" : true, "allowEdgeOverflow" : false});
        }
        {
            var Q0;
            Q0=makeQuery(id+"F28.opExtrude","CAP_FACE",FACE,{"disambiguationData":[OSD([sQuery(id+"F27.wireOp",EDGE,"E59"),sQuery(id+"F27.wireOp",EDGE,"E60"),sQuery(id+"F27.wireOp",EDGE,"E61"),sQuery(id+"F27.wireOp",EDGE,"E62")])],"isStart":true});
            var sketch = newSketch(context, id + "F30", { "sketchPlane" : qUnion([Q0])});
            skLineSegment(sketch, "E63.bottom", {"start": v(-546.1, 558.8) * mm, "end": v(-952.5, 558.8) * mm});
            skLineSegment(sketch, "E63.top", {"start": v(-546.1, 1270) * mm, "end": v(-952.5, 1270) * mm});
            skLineSegment(sketch, "E63.left", {"start": v(-546.1, 558.8) * mm, "end": v(-546.1, 1270) * mm});
            skLineSegment(sketch, "E63.right", {"start": v(-952.5, 558.8) * mm, "end": v(-952.5, 1270) * mm});
            skSolve(sketch);
        }
        {
            var Q0;
            Q0=qSketchRegion(id+"F30",true);
            extrude(context, id + "F31", {"entities" : qUnion([Q0]), "depth" : 50.8 * mm});
        }
        {
            var Q0;
            Q0=makeQuery(id+"F31.opExtrude","CAP_FACE",FACE,{"disambiguationData":[OSD([sQuery(id+"F30.wireOp",EDGE,"E63.bottom"),sQuery(id+"F30.wireOp",EDGE,"E63.top"),sQuery(id+"F30.wireOp",EDGE,"E63.left"),sQuery(id+"F30.wireOp",EDGE,"E63.right")])],"isStart":true});
            var sketch = newSketch(context, id + "F32", { "sketchPlane" : qUnion([Q0])});
            skLineSegment(sketch, "E64.bottom", {"start": v(546.1, 1270) * mm, "end": v(565.15, 1270) * mm});
            skLineSegment(sketch, "E64.top", {"start": v(546.1, 577.85) * mm, "end": v(565.15, 577.85) * mm});
            skLineSegment(sketch, "E64.left", {"start": v(546.1, 1270) * mm, "end": v(546.1, 577.85) * mm});
            skLineSegment(sketch, "E64.right", {"start": v(565.15, 1270) * mm, "end": v(565.15, 577.85) * mm});
            skLineSegment(sketch, "E65.bottom", {"start": v(952.5, 1270) * mm, "end": v(933.45, 1270) * mm});
            skLineSegment(sketch, "E65.top", {"start": v(952.5, 577.85) * mm, "end": v(933.45, 577.85) * mm});
            skLineSegment(sketch, "E65.left", {"start": v(952.5, 1270) * mm, "end": v(952.5, 577.85) * mm});
            skLineSegment(sketch, "E65.right", {"start": v(933.45, 1270) * mm, "end": v(933.45, 577.85) * mm});
            skLineSegment(sketch, "E66.bottom", {"start": v(565.15, 577.85) * mm, "end": v(742.95, 577.85) * mm});
            skLineSegment(sketch, "E66.top", {"start": v(565.15, 755.65) * mm, "end": v(742.95, 755.65) * mm});
            skLineSegment(sketch, "E66.left", {"start": v(565.15, 577.85) * mm, "end": v(565.15, 755.65) * mm});
            skLineSegment(sketch, "E66.right", {"start": v(742.95, 577.85) * mm, "end": v(742.95, 755.65) * mm});
            skLineSegment(sketch, "E67.bottom", {"start": v(933.45, 577.85) * mm, "end": v(755.65, 577.85) * mm});
            skLineSegment(sketch, "E67.top", {"start": v(933.45, 755.65) * mm, "end": v(755.65, 755.65) * mm});
            skLineSegment(sketch, "E67.left", {"start": v(933.45, 577.85) * mm, "end": v(933.45, 755.65) * mm});
            skLineSegment(sketch, "E67.right", {"start": v(755.65, 577.85) * mm, "end": v(755.65, 755.65) * mm});
            skLineSegment(sketch, "E68.0.1.0", {"start": v(565.15, 946.15) * mm, "end": v(742.95, 946.15) * mm});
            skLineSegment(sketch, "E68.0.1.1", {"start": v(565.15, 768.35) * mm, "end": v(742.95, 768.35) * mm});
            skLineSegment(sketch, "E68.0.1.2", {"start": v(742.95, 768.35) * mm, "end": v(742.95, 946.15) * mm});
            skLineSegment(sketch, "E68.0.1.3", {"start": v(755.65, 768.35) * mm, "end": v(755.65, 946.15) * mm});
            skLineSegment(sketch, "E68.0.1.4", {"start": v(933.45, 946.15) * mm, "end": v(755.65, 946.15) * mm});
            skLineSegment(sketch, "E68.0.1.5", {"start": v(933.45, 1460.5) * mm, "end": v(933.45, 768.35) * mm});
            skLineSegment(sketch, "E68.0.1.6", {"start": v(933.45, 768.35) * mm, "end": v(755.65, 768.35) * mm});
            skLineSegment(sketch, "E68.0.2.0", {"start": v(565.15, 1136.65) * mm, "end": v(742.95, 1136.65) * mm});
            skLineSegment(sketch, "E68.0.2.1", {"start": v(565.15, 958.85) * mm, "end": v(742.95, 958.85) * mm});
            skLineSegment(sketch, "E68.0.2.2", {"start": v(742.95, 958.85) * mm, "end": v(742.95, 1136.65) * mm});
            skLineSegment(sketch, "E68.0.2.3", {"start": v(755.65, 958.85) * mm, "end": v(755.65, 1136.65) * mm});
            skLineSegment(sketch, "E68.0.2.4", {"start": v(933.45, 1136.65) * mm, "end": v(755.65, 1136.65) * mm});
            skLineSegment(sketch, "E68.0.2.5", {"start": v(933.45, 1651) * mm, "end": v(933.45, 958.85) * mm});
            skLineSegment(sketch, "E68.0.2.6", {"start": v(933.45, 958.85) * mm, "end": v(755.65, 958.85) * mm});
            skLineSegment(sketch, "E68.direction1", {"start": v(565.15, 755.65) * mm, "end": v(590.55, 755.65) * mm, "construction": true});
            skLineSegment(sketch, "E68.direction2", {"start": v(565.15, 755.65) * mm, "end": v(565.15, 946.15) * mm, "construction": true});
            skLineSegment(sketch, "E69", {"start": v(565.15, 1136.65) * mm, "end": v(565.15, 1149.35) * mm});
            skLineSegment(sketch, "E70", {"start": v(565.15, 1149.35) * mm, "end": v(933.45, 1149.35) * mm});
            skSolve(sketch);
        }
        {
            var Q0;
            {var subQ3=sQuery(id+"F32.wireOp",EDGE,"E70");Q0=makeQuery(id+"F32.imprint","IMPRINT",FACE,{"disambiguationData":[TD([[makeQuery(id+"F32.imprint","IMPRINT",EDGE,{"derivedFrom":subQ3}),1.0]])]});}
            var Q1;
            {var subQ0=sQuery(id+"F32.wireOp",EDGE,"E68.0.2.0");Q1=makeQuery(id+"F32.imprint","IMPRINT",FACE,{"disambiguationData":[TD([[makeQuery(id+"F32.imprint","IMPRINT",EDGE,{"derivedFrom":subQ0}),-1.0]])]});}
            var Q2;
            Q2=makeQuery(id+"F32.imprint","IMPRINT",FACE,{"disambiguationData":[TD([[makeQuery(id+"F32.imprint","IMPRINT",EDGE,{"derivedFrom":sQuery(id+"F32.wireOp",EDGE,"E68.0.2.3")}),-1.0]])]});
            var Q3;
            Q3=makeQuery(id+"F32.imprint","IMPRINT",FACE,{"disambiguationData":[TD([[makeQuery(id+"F32.imprint","IMPRINT",EDGE,{"derivedFrom":sQuery(id+"F32.wireOp",EDGE,"E68.0.1.3")}),-1.0]])]});
            var Q4;
            {var subQ0=sQuery(id+"F32.wireOp",EDGE,"E68.0.1.0");Q4=makeQuery(id+"F32.imprint","IMPRINT",FACE,{"disambiguationData":[TD([[makeQuery(id+"F32.imprint","IMPRINT",EDGE,{"derivedFrom":subQ0}),-1.0]])]});}
            var Q5;
            Q5=makeQuery(id+"F32.imprint","IMPRINT",FACE,{"disambiguationData":[TD([[makeQuery(id+"F32.imprint","IMPRINT",EDGE,{"derivedFrom":sQuery(id+"F32.wireOp",EDGE,"E66.bottom")}),1.0]])]});
            var Q6;
            Q6=makeQuery(id+"F32.imprint","IMPRINT",FACE,{"disambiguationData":[TD([[makeQuery(id+"F32.imprint","IMPRINT",EDGE,{"derivedFrom":sQuery(id+"F32.wireOp",EDGE,"E67.bottom")}),-1.0]])]});
            extrude(context, id + "F33", {"entities" : qUnion([Q0, Q1, Q2, Q3, Q4, Q5, Q6]), "operationType" : NewBodyOperationType.REMOVE, "oppositeDirection" : true, "depth" : 44.45 * mm});
        }
    });
